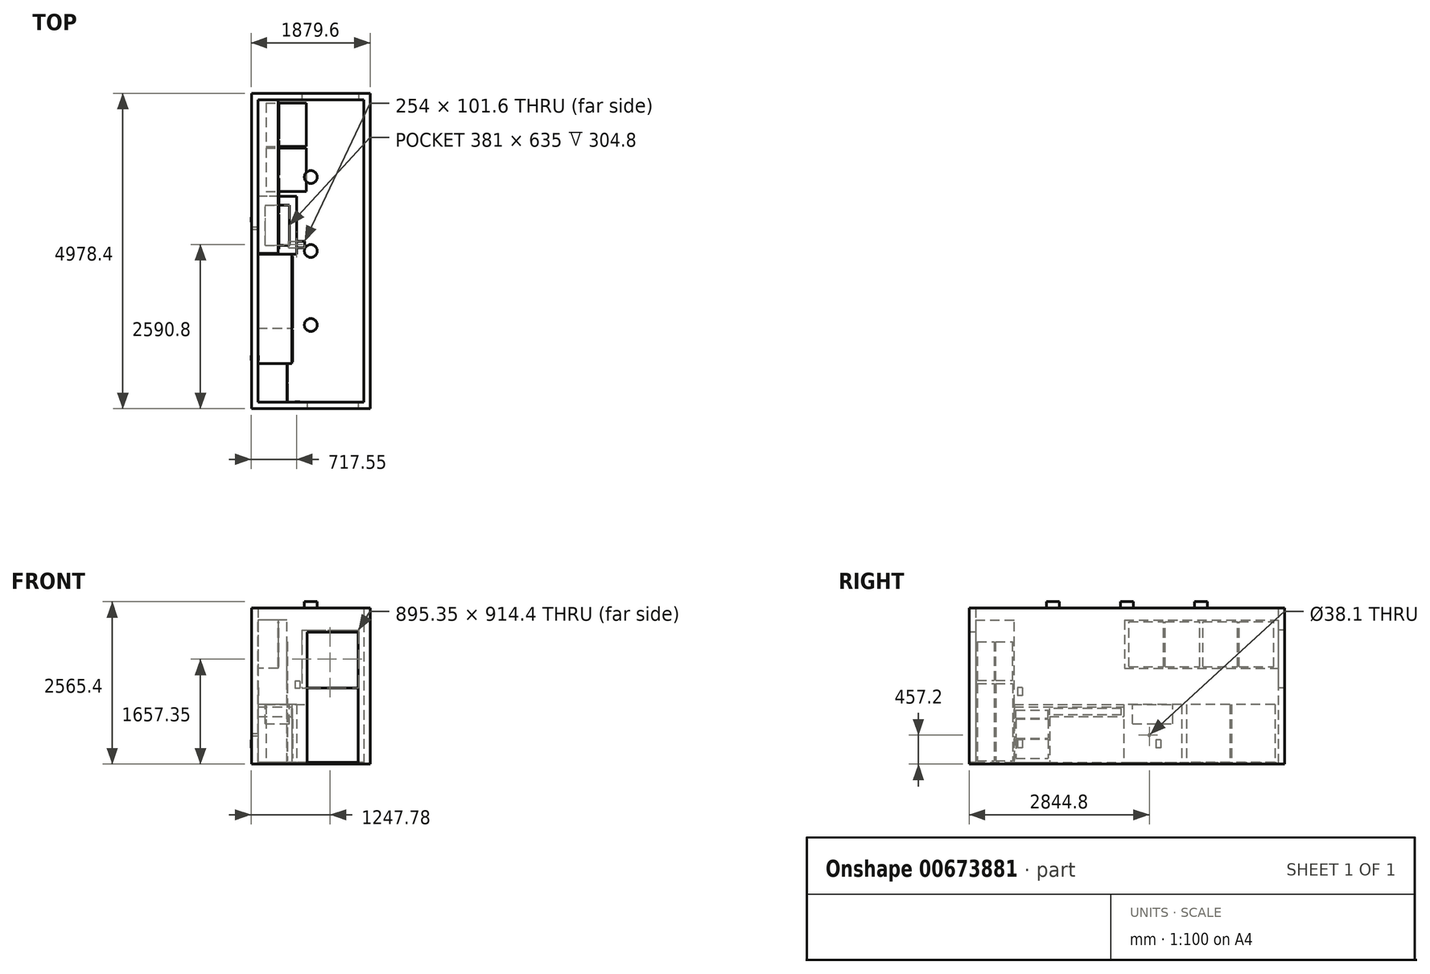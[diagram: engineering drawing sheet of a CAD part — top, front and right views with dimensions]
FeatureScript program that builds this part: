
annotation { "Feature Type Name" : "Feature", "Feature Type Description" : "" }
export const myFeature = defineFeature(function(context is Context, id is Id, definition is map)
    precondition{}
    {
        {
            var Q0;
            Q0=qCreatedBy(makeId("Top.planeOp"),FACE);
            var sketch = newSketch(context, id + "F0", { "sketchPlane" : qUnion([Q0])});
            skLineSegment(sketch, "E0.bottom", {"start": v(0, 0) * mm, "end": v(-1670.05, 0) * mm});
            skLineSegment(sketch, "E0.top", {"start": v(0, 4775.2) * mm, "end": v(-1670.05, 4775.2) * mm});
            skLineSegment(sketch, "E0.left", {"start": v(0, 0) * mm, "end": v(0, 4775.2) * mm});
            skLineSegment(sketch, "E0.right", {"start": v(-1670.05, 0) * mm, "end": v(-1670.05, 4775.2) * mm});
            skLineSegment(sketch, "E1.0", {"start": v(-1771.65, -101.6) * mm, "end": v(-1771.65, 4876.8) * mm});
            skLineSegment(sketch, "E1.1", {"start": v(101.6, -101.6) * mm, "end": v(-1771.65, -101.6) * mm});
            skLineSegment(sketch, "E1.2", {"start": v(101.6, -101.6) * mm, "end": v(101.6, 4876.8) * mm});
            skLineSegment(sketch, "E1.3", {"start": v(101.6, 4876.8) * mm, "end": v(-1771.65, 4876.8) * mm});
            skSolve(sketch);
        }
        {
            var Q0;
            Q0=qSketchRegion(id+"F0",true);
            extrude(context, id + "F1", {"entities" : qUnion([Q0]), "depth" : 2438.4 * mm, "offsetDistance" : 25.4 * mm});
        }
        {
            var Q0;
            Q0=makeQuery(id+"F1.opExtrude","SWEPT_FACE",FACE,{"disambiguationData":[OSD([sQuery(id+"F0.wireOp",EDGE,"E1.1")])]});
            var sketch = newSketch(context, id + "F2", { "sketchPlane" : qUnion([Q0])});
            skLineSegment(sketch, "E2.bottom", {"start": v(-88.9, 0) * mm, "end": v(-895.35, 0) * mm});
            skLineSegment(sketch, "E2.top", {"start": v(-88.9, 2057.4) * mm, "end": v(-895.35, 2057.4) * mm});
            skLineSegment(sketch, "E2.left", {"start": v(-88.9, 0) * mm, "end": v(-88.9, 2057.4) * mm});
            skLineSegment(sketch, "E2.right", {"start": v(-895.35, 0) * mm, "end": v(-895.35, 2057.4) * mm});
            skSolve(sketch);
        }
        {
            var Q0;
            Q0=qSketchRegion(id+"F2",true);
            extrude(context, id + "F3", {"entities" : qUnion([Q0]), "operationType" : NewBodyOperationType.REMOVE, "endBound" : BoundingType.UP_TO_NEXT, "oppositeDirection" : true, "depth" : 25.4 * mm, "offsetDistance" : 25.4 * mm});
        }
        {
            var Q0;
            Q0=makeQuery(id+"F1.opExtrude","SWEPT_FACE",FACE,{"disambiguationData":[OSD([sQuery(id+"F0.wireOp",EDGE,"E0.top")])]});
            var sketch = newSketch(context, id + "F4", { "sketchPlane" : qUnion([Q0])});
            skLineSegment(sketch, "E3.bottom", {"start": v(-977.9, 2089.15) * mm, "end": v(-82.55, 2089.15) * mm});
            skLineSegment(sketch, "E3.top", {"start": v(-977.9, 1174.75) * mm, "end": v(-82.55, 1174.75) * mm});
            skLineSegment(sketch, "E3.left", {"start": v(-977.9, 2089.15) * mm, "end": v(-977.9, 1174.75) * mm});
            skLineSegment(sketch, "E3.right", {"start": v(-82.55, 2089.15) * mm, "end": v(-82.55, 1174.75) * mm});
            skSolve(sketch);
        }
        {
            var Q0;
            Q0=qSketchRegion(id+"F4",true);
            extrude(context, id + "F5", {"entities" : qUnion([Q0]), "operationType" : NewBodyOperationType.REMOVE, "endBound" : BoundingType.UP_TO_NEXT, "oppositeDirection" : true, "depth" : 25.4 * mm, "offsetDistance" : 25.4 * mm});
        }
        {
            var Q0;
            Q0=makeQuery(id+"F1.opExtrude","CAP_FACE",FACE,{"disambiguationData":[OSD([sQuery(id+"F0.wireOp",EDGE,"E0.bottom"),sQuery(id+"F0.wireOp",EDGE,"E0.top"),sQuery(id+"F0.wireOp",EDGE,"E0.left"),sQuery(id+"F0.wireOp",EDGE,"E0.right"),sQuery(id+"F0.wireOp",EDGE,"E1.0"),sQuery(id+"F0.wireOp",EDGE,"E1.1"),sQuery(id+"F0.wireOp",EDGE,"E1.2"),sQuery(id+"F0.wireOp",EDGE,"E1.3")])],"isStart":true});
            var sketch = newSketch(context, id + "F6", { "sketchPlane" : qUnion([Q0])});
            skLineSegment(sketch, "E4.bottom", {"start": v(101.6, 101.6) * mm, "end": v(-1771.65, 101.6) * mm});
            skLineSegment(sketch, "E4.top", {"start": v(101.6, -4876.8) * mm, "end": v(-1771.65, -4876.8) * mm});
            skLineSegment(sketch, "E4.left", {"start": v(101.6, 101.6) * mm, "end": v(101.6, -4876.8) * mm});
            skLineSegment(sketch, "E4.right", {"start": v(-1771.65, 101.6) * mm, "end": v(-1771.65, -4876.8) * mm});
            skLineSegment(sketch, "E5.bottom", {"start": v(-1187.45, -2438.4) * mm, "end": v(-933.45, -2438.4) * mm});
            skLineSegment(sketch, "E5.top", {"start": v(-1187.45, -2540) * mm, "end": v(-933.45, -2540) * mm});
            skLineSegment(sketch, "E5.left", {"start": v(-1187.45, -2438.4) * mm, "end": v(-1187.45, -2540) * mm});
            skLineSegment(sketch, "E5.right", {"start": v(-933.45, -2438.4) * mm, "end": v(-933.45, -2540) * mm});
            skSolve(sketch);
        }
        {
            var Q0;
            Q0=qSketchRegion(id+"F6",true);
            extrude(context, id + "F7", {"entities" : qUnion([Q0]), "operationType" : NewBodyOperationType.ADD, "depth" : 25.4 * mm, "offsetDistance" : 25.4 * mm});
        }
        {
            var Q0;
            Q0=makeQuery(id+"F7.opExtrude","CAP_FACE",FACE,{"disambiguationData":[OSD([sQuery(id+"F6.wireOp",EDGE,"E4.bottom"),sQuery(id+"F6.wireOp",EDGE,"E4.top"),sQuery(id+"F6.wireOp",EDGE,"E4.left"),sQuery(id+"F6.wireOp",EDGE,"E4.right")])],"isStart":true});
            var sketch = newSketch(context, id + "F8", { "sketchPlane" : qUnion([Q0])});
            skLineSegment(sketch, "E6.bottom", {"start": v(-1543.05, 4724.4) * mm, "end": v(-908.05, 4724.4) * mm});
            skLineSegment(sketch, "E6.top", {"start": v(-1543.05, 4038.6) * mm, "end": v(-908.05, 4038.6) * mm});
            skLineSegment(sketch, "E6.left", {"start": v(-1543.05, 4724.4) * mm, "end": v(-1543.05, 4038.6) * mm});
            skLineSegment(sketch, "E6.right", {"start": v(-908.05, 4724.4) * mm, "end": v(-908.05, 4038.6) * mm});
            skLineSegment(sketch, "E7.bottom", {"start": v(-1543.05, 4013.2) * mm, "end": v(-908.05, 4013.2) * mm});
            skLineSegment(sketch, "E7.top", {"start": v(-1543.05, 3327.4) * mm, "end": v(-908.05, 3327.4) * mm});
            skLineSegment(sketch, "E7.left", {"start": v(-1543.05, 4013.2) * mm, "end": v(-1543.05, 3327.4) * mm});
            skLineSegment(sketch, "E7.right", {"start": v(-908.05, 4013.2) * mm, "end": v(-908.05, 3327.4) * mm});
            skSolve(sketch);
        }
        {
            var Q0;
            Q0=qSketchRegion(id+"F8",true);
            extrude(context, id + "F9", {"entities" : qUnion([Q0]), "depth" : 914.4 * mm, "offsetDistance" : 25.4 * mm});
        }
        {
            var Q0;
            {var subQ0=sQuery(id+"F0.wireOp",EDGE,"E0.top");var subQ5=sQuery(id+"F0.wireOp",EDGE,"E0.right");Q0=makeQuery(id+"FF5OUzfLRYdxron_1.boolean.opBoolean","SPLIT",FACE,{"disambiguationData":[TD([makeQuery(id+"F1.opExtrude","SWEPT_FACE",FACE,{"disambiguationData":[OSD([subQ0])]})])],"derivedFrom":makeQuery(id+"F1.opExtrude","SWEPT_FACE",FACE,{"disambiguationData":[OSD([subQ5])]})});}
            var sketch = newSketch(context, id + "F10", { "sketchPlane" : qUnion([Q0])});
            skLineSegment(sketch, "E8.top", {"start": v(2349.5, 1485.9) * mm, "end": v(4775.2, 1485.9) * mm});
            skLineSegment(sketch, "E8.left", {"start": v(2349.5, 2247.9) * mm, "end": v(2349.5, 1485.9) * mm});
            skLineSegment(sketch, "E8.right", {"start": v(4775.2, 2247.9) * mm, "end": v(4775.2, 1485.9) * mm});
            skLineSegment(sketch, "E9", {"start": v(2349.5, 2247.9) * mm, "end": v(4775.2, 2247.9) * mm});
            skSolve(sketch);
        }
        {
            var Q0;
            Q0=qSketchRegion(id+"F10",true);
            extrude(context, id + "F11", {"entities" : qUnion([Q0]), "depth" : 317.5 * mm, "offsetDistance" : 25.4 * mm});
        }
        {
            var Q0;
            Q0=makeQuery(id+"F7.boolean.opBoolean","MERGE",FACE,{"derivedFrom":[makeQuery(id+"F1.opExtrude","SWEPT_FACE",FACE,{"disambiguationData":[OSD([sQuery(id+"F0.wireOp",EDGE,"E1.0")])]}),makeQuery(id+"F7.opExtrude","SWEPT_FACE",FACE,{"disambiguationData":[OSD([sQuery(id+"F6.wireOp",EDGE,"E4.right")])]})]});
            var sketch = newSketch(context, id + "F12", { "sketchPlane" : qUnion([Q0])});
            skCircle(sketch, "E10", {"center": v(-2743.2, 431.8) * mm, "radius": 19.05 * mm});
            skSolve(sketch);
        }
        {
            var Q0;
            Q0=makeQuery(id+"F1.opExtrude","SWEPT_FACE",FACE,{"disambiguationData":[OSD([sQuery(id+"F0.wireOp",EDGE,"E0.bottom")])]});
            var sketch = newSketch(context, id + "F13", { "sketchPlane" : qUnion([Q0])});
            skLineSegment(sketch, "E11.bottom", {"start": v(1009.65, 1282.7) * mm, "end": v(1085.85, 1282.7) * mm});
            skLineSegment(sketch, "E11.top", {"start": v(1009.65, 1168.4) * mm, "end": v(1085.85, 1168.4) * mm});
            skLineSegment(sketch, "E11.left", {"start": v(1009.65, 1282.7) * mm, "end": v(1009.65, 1168.4) * mm});
            skLineSegment(sketch, "E11.right", {"start": v(1085.85, 1282.7) * mm, "end": v(1085.85, 1168.4) * mm});
            skSolve(sketch);
        }
        {
            var Q0;
            Q0=qSketchRegion(id+"F13",true);
            extrude(context, id + "F14", {"entities" : qUnion([Q0]), "depth" : 6.35 * mm, "offsetDistance" : 25.4 * mm});
        }
        {
            var Q0;
            {var subQ0=sQuery(id+"F0.wireOp",EDGE,"E1.3");var subQ1=sQuery(id+"F0.wireOp",EDGE,"E1.2");var subQ2=sQuery(id+"F0.wireOp",EDGE,"E1.1");var subQ3=sQuery(id+"F0.wireOp",EDGE,"E1.0");var subQ4=sQuery(id+"F0.wireOp",EDGE,"E0.right");var subQ5=sQuery(id+"F0.wireOp",EDGE,"E0.left");var subQ6=sQuery(id+"F0.wireOp",EDGE,"E0.top");var subQ7=sQuery(id+"F0.wireOp",EDGE,"E0.bottom");Q0=makeQuery(id+"F6lEAw4BziHLS6e_1.boolean.opBoolean","MERGE",FACE,{"derivedFrom":[makeQuery(id+"FF5OUzfLRYdxron_1.boolean.opBoolean","MERGE",FACE,{"derivedFrom":[makeQuery(id+"F1.opExtrude","CAP_FACE",FACE,{"disambiguationData":[OSD([subQ7,subQ6,subQ5,subQ4,subQ3,subQ2,subQ1,subQ0])],"isStart":false}),makeQuery(id+"FF5OUzfLRYdxron_1.opExtrude","CAP_FACE",FACE,{"disambiguationData":[OSD([subQ7,subQ6,subQ5,subQ4,subQ3,subQ2,subQ1,subQ0]),OD(0.0)],"isStart":false}),makeQuery(id+"FF5OUzfLRYdxron_1.opExtrude","CAP_FACE",FACE,{"disambiguationData":[OSD([subQ7,subQ6,subQ5,subQ4,subQ3,subQ2,subQ1,subQ0]),OD(1.0)],"isStart":false})]}),makeQuery(id+"F6lEAw4BziHLS6e_1.opExtrude","SWEPT_FACE",FACE,{"disambiguationData":[OSD([sQuery(id+"FKdh9NI14bl7I8A_1.wireOp",EDGE,"L0rorLmK-Bkry-kT8l-oB2h-IIx823DkUJX5.bottom")])]})]});}
            var sketch = newSketch(context, id + "F15", { "sketchPlane" : qUnion([Q0])});
            skCircle(sketch, "E12", {"center": v(-835.03, 3556) * mm, "radius": 101.6 * mm});
            skCircle(sketch, "E13", {"center": v(-835.03, 1219.2) * mm, "radius": 101.6 * mm});
            skLineSegment(sketch, "E14", {"start": v(-1670.05, 3556) * mm, "end": v(-835.03, 3556) * mm, "construction": true});
            skLineSegment(sketch, "E15", {"start": v(0, 3556) * mm, "end": v(-835.03, 3556) * mm, "construction": true});
            skLineSegment(sketch, "E16", {"start": v(0, 1219.2) * mm, "end": v(-1670.05, 1219.2) * mm, "construction": true});
            skLineSegment(sketch, "E17", {"start": v(-835.03, 1219.2) * mm, "end": v(-835.03, 0) * mm, "construction": true});
            skCircle(sketch, "E18", {"center": v(-835.03, 2387.6) * mm, "radius": 101.6 * mm});
            skLineSegment(sketch, "E19", {"start": v(-835.03, 1219.2) * mm, "end": v(-835.03, 3556) * mm, "construction": true});
            skSolve(sketch);
        }
        {
            var Q0;
            Q0=qSketchRegion(id+"F15",true);
            extrude(context, id + "F16", {"entities" : qUnion([Q0]), "depth" : 101.6 * mm, "offsetDistance" : 25.4 * mm});
        }
        {
            var Q0;
            Q0=makeQuery(id+"F1.opExtrude","SWEPT_FACE",FACE,{"disambiguationData":[OSD([sQuery(id+"F0.wireOp",EDGE,"E0.right")])]});
            var sketch = newSketch(context, id + "F17", { "sketchPlane" : qUnion([Q0])});
            skLineSegment(sketch, "E20.bottom", {"start": v(0, 0) * mm, "end": v(609.6, 0) * mm});
            skLineSegment(sketch, "E20.top", {"start": v(0, 2438.4) * mm, "end": v(0, 2438.4) * mm});
            skLineSegment(sketch, "E20.left", {"start": v(0, 0) * mm, "end": v(0, 2438.4) * mm});
            skLineSegment(sketch, "E20.right", {"start": v(609.6, 0) * mm, "end": v(609.6, 2247.9) * mm});
            skLineSegment(sketch, "E21", {"start": v(0, 2247.9) * mm, "end": v(0, 0) * mm});
            skLineSegment(sketch, "E22", {"start": v(0, 2247.9) * mm, "end": v(609.6, 2247.9) * mm});
            skSolve(sketch);
        }
        {
            var Q0;
            {var subQ0=sQuery(id+"F17.wireOp",EDGE,"E20.right");Q0=makeQuery(id+"F17.imprint","IMPRINT",FACE,{"disambiguationData":[TD([[makeQuery(id+"F17.imprint","IMPRINT",EDGE,{"derivedFrom":subQ0}),1.0]])]});}
            extrude(context, id + "F18", {"entities" : qUnion([Q0]), "depth" : 457.2 * mm, "offsetDistance" : 25.4 * mm});
        }
        {
            var Q0;
            Q0=makeQuery(id+"F1.opExtrude","SWEPT_FACE",FACE,{"disambiguationData":[OSD([sQuery(id+"F0.wireOp",EDGE,"E0.right")])]});
            var sketch = newSketch(context, id + "F19", { "sketchPlane" : qUnion([Q0])});
            skLineSegment(sketch, "E23.bottom", {"start": v(3251.2, 914.4) * mm, "end": v(2336.8, 914.4) * mm});
            skLineSegment(sketch, "E23.top", {"start": v(3251.2, 0) * mm, "end": v(2336.8, 0) * mm});
            skLineSegment(sketch, "E23.left", {"start": v(3251.2, 914.4) * mm, "end": v(3251.2, 0) * mm});
            skLineSegment(sketch, "E23.right", {"start": v(2336.8, 914.4) * mm, "end": v(2336.8, 0) * mm});
            skSolve(sketch);
        }
        {
            var Q0;
            Q0 = qSketchRegion(id + "F19", true);
            extrude(context, id + "F20", {"entities" : qUnion([Q0]), "depth" : 609.6 * mm, "offsetDistance" : 25.4 * mm});
        }
        {
            var Q0;
            Q0=makeQuery(id+"F1.opExtrude","SWEPT_FACE",FACE,{"disambiguationData":[OSD([sQuery(id+"F0.wireOp",EDGE,"E0.right")])]});
            var sketch = newSketch(context, id + "F21", { "sketchPlane" : qUnion([Q0])});
            skLineSegment(sketch, "E24.0.0", {"start": v(609.6, 0) * mm, "end": v(609.6, 0) * mm});
            skLineSegment(sketch, "E24.0.2", {"start": v(609.6, 0) * mm, "end": v(609.6, 0) * mm});
            skLineSegment(sketch, "E25.bottom", {"start": v(609.6, 914.4) * mm, "end": v(2336.8, 914.4) * mm});
            skLineSegment(sketch, "E25.top", {"start": v(609.6, 876.3) * mm, "end": v(2336.8, 876.3) * mm});
            skLineSegment(sketch, "E25.left", {"start": v(609.6, 914.4) * mm, "end": v(609.6, 876.3) * mm});
            skLineSegment(sketch, "E25.right", {"start": v(2336.8, 914.4) * mm, "end": v(2336.8, 876.3) * mm});
            skSolve(sketch);
        }
        {
            var Q0;
            Q0 = qSketchRegion(id + "F21", true);
            extrude(context, id + "F22", {"entities" : qUnion([Q0]), "depth" : 533.4 * mm, "offsetDistance" : 25.4 * mm});
        }
        {
            var Q0;
            Q0=makeQuery(id+"FyeGjvqHZ8qtpXd_9.boolean.opBoolean","MERGE",FACE,{"derivedFrom":[makeQuery(id+"F22.opExtrude","CAP_FACE",FACE,{"disambiguationData":[OSD([sQuery(id+"F21.wireOp",EDGE,"E25.bottom"),sQuery(id+"F21.wireOp",EDGE,"E25.top"),sQuery(id+"F21.wireOp",EDGE,"E25.left"),sQuery(id+"F21.wireOp",EDGE,"E25.right")])],"isStart":false}),makeQuery(id+"FyeGjvqHZ8qtpXd_9.opExtrude","SWEPT_FACE",FACE,{"disambiguationData":[OSD([sQuery(id+"F46rnMOmZh9QJuk_9.wireOp",EDGE,"LmVa3B9K-5IW6-0650-ylxf-dCjXZTulEtGs.left")])]})]});
            var sketch = newSketch(context, id + "F23", { "sketchPlane" : qUnion([Q0])});
            skLineSegment(sketch, "E26.bottom", {"start": v(609.6, 876.3) * mm, "end": v(1168.4, 876.3) * mm});
            skLineSegment(sketch, "E26.top", {"start": v(609.6, 0) * mm, "end": v(1168.4, 0) * mm});
            skLineSegment(sketch, "E26.left", {"start": v(609.6, 876.3) * mm, "end": v(609.6, 0) * mm});
            skLineSegment(sketch, "E26.right", {"start": v(1168.4, 876.3) * mm, "end": v(1168.4, 0) * mm});
            skLineSegment(sketch, "E27.0", {"start": v(2336.8, 914.4) * mm, "end": v(2336.8, 0) * mm});
            skLineSegment(sketch, "E28.bottom", {"start": v(1168.4, 876.3) * mm, "end": v(2336.8, 876.3) * mm});
            skLineSegment(sketch, "E28.top", {"start": v(1168.4, 723.9) * mm, "end": v(2336.8, 723.9) * mm});
            skLineSegment(sketch, "E28.left", {"start": v(1168.4, 876.3) * mm, "end": v(1168.4, 723.9) * mm});
            skLineSegment(sketch, "E28.right", {"start": v(2336.8, 876.3) * mm, "end": v(2336.8, 723.9) * mm});
            skSolve(sketch);
        }
        {
            var Q0;
            Q0 = qSketchRegion(id + "F23", true);
            extrude(context, id + "F24", {"entities" : qUnion([Q0]), "endBound" : BoundingType.UP_TO_NEXT, "oppositeDirection" : true, "depth" : 25.4 * mm, "offsetDistance" : 25.4 * mm});
        }
        {
            var Q0;
            Q0=makeQuery(id+"F24.opExtrude","CAP_FACE",FACE,{"disambiguationData":[OSD([sQuery(id+"F23.wireOp",EDGE,"E26.bottom"),sQuery(id+"F23.wireOp",EDGE,"E26.top"),sQuery(id+"F23.wireOp",EDGE,"E26.left"),sQuery(id+"F23.wireOp",EDGE,"E26.right")])],"isStart":true});
            var sketch = newSketch(context, id + "F25", { "sketchPlane" : qUnion([Q0])});
            skLineSegment(sketch, "E29.bottom", {"start": v(635, 368.3) * mm, "end": v(1143, 368.3) * mm});
            skLineSegment(sketch, "E29.top", {"start": v(635, 63.5) * mm, "end": v(1143, 63.5) * mm});
            skLineSegment(sketch, "E29.left", {"start": v(635, 368.3) * mm, "end": v(635, 63.5) * mm});
            skLineSegment(sketch, "E29.right", {"start": v(1143, 368.3) * mm, "end": v(1143, 63.5) * mm});
            skLineSegment(sketch, "E30.bottom", {"start": v(635, 685.8) * mm, "end": v(1143, 685.8) * mm});
            skLineSegment(sketch, "E30.top", {"start": v(635, 381) * mm, "end": v(1143, 381) * mm});
            skLineSegment(sketch, "E30.left", {"start": v(635, 685.8) * mm, "end": v(635, 381) * mm});
            skLineSegment(sketch, "E30.right", {"start": v(1143, 685.8) * mm, "end": v(1143, 381) * mm});
            skLineSegment(sketch, "E31.bottom", {"start": v(635, 698.5) * mm, "end": v(1143, 698.5) * mm});
            skLineSegment(sketch, "E31.top", {"start": v(635, 825.5) * mm, "end": v(1143, 825.5) * mm});
            skLineSegment(sketch, "E31.left", {"start": v(635, 698.5) * mm, "end": v(635, 825.5) * mm});
            skLineSegment(sketch, "E31.right", {"start": v(1143, 698.5) * mm, "end": v(1143, 825.5) * mm});
            skLineSegment(sketch, "E32", {"start": v(1143, 698.5) * mm, "end": v(1143, 685.8) * mm, "construction": true});
            skLineSegment(sketch, "E33", {"start": v(1143, 381) * mm, "end": v(1143, 368.3) * mm, "construction": true});
            skLineSegment(sketch, "E34", {"start": v(609.6, 825.5) * mm, "end": v(635, 825.5) * mm, "construction": true});
            skLineSegment(sketch, "E35", {"start": v(1143, 825.5) * mm, "end": v(1168.4, 825.5) * mm, "construction": true});
            skLineSegment(sketch, "E36.left", {"start": v(1168.4, 0) * mm, "end": v(1168.4, -177.8) * mm});
            skLineSegment(sketch, "E37.bottom", {"start": v(2302.58, 750.93) * mm, "end": v(1168.4, 750.93) * mm});
            skLineSegment(sketch, "E37.top", {"start": v(2302.58, 855.12) * mm, "end": v(1168.4, 855.12) * mm});
            skLineSegment(sketch, "E37.left", {"start": v(2302.58, 750.93) * mm, "end": v(2302.58, 855.12) * mm});
            skLineSegment(sketch, "E37.right", {"start": v(1168.4, 750.93) * mm, "end": v(1168.4, 855.12) * mm});
            skSolve(sketch);
        }
        {
            var Q0;
            Q0 = qSketchRegion(id + "F25", true);
            extrude(context, id + "F26", {"entities" : qUnion([Q0]), "operationType" : NewBodyOperationType.ADD, "depth" : 12.7 * mm, "offsetDistance" : 25.4 * mm});
        }
        {
            var Q0;
            Q0 = qSketchRegion(id + "F12", true);
            var Q1;
            Q1=makeQuery(id+"F1.opExtrude","SWEPT_FACE",FACE,{"disambiguationData":[OSD([sQuery(id+"F0.wireOp",EDGE,"E0.right")])]});
            extrude(context, id + "F27", {"entities" : qUnion([Q0]), "operationType" : NewBodyOperationType.REMOVE, "endBound" : BoundingType.UP_TO_SURFACE, "oppositeDirection" : true, "depth" : 25.4 * mm, "endBoundEntityFace" : qUnion([Q1]), "offsetDistance" : 25.4 * mm});
        }
        {
            var Q0;
            Q0=makeQuery(id+"F18.opExtrude","CAP_FACE",FACE,{"disambiguationData":[OSD([sQuery(id+"F17.wireOp",EDGE,"E20.bottom"),sQuery(id+"F17.wireOp",EDGE,"E20.top"),sQuery(id+"F17.wireOp",EDGE,"E20.right"),sQuery(id+"F17.wireOp",EDGE,"E21")])],"isStart":false});
            var sketch = newSketch(context, id + "F28", { "sketchPlane" : qUnion([Q0])});
            skLineSegment(sketch, "E38.bottom", {"start": v(25.4, 1244.6) * mm, "end": v(292.1, 1244.6) * mm});
            skLineSegment(sketch, "E38.top", {"start": v(25.4, 25.4) * mm, "end": v(292.1, 25.4) * mm});
            skLineSegment(sketch, "E38.left", {"start": v(25.4, 1244.6) * mm, "end": v(25.4, 25.4) * mm});
            skLineSegment(sketch, "E38.right", {"start": v(292.1, 1244.6) * mm, "end": v(292.1, 25.4) * mm});
            skLineSegment(sketch, "E39.bottom", {"start": v(317.5, 1244.6) * mm, "end": v(584.2, 1244.6) * mm});
            skLineSegment(sketch, "E39.top", {"start": v(317.5, 25.4) * mm, "end": v(584.2, 25.4) * mm});
            skLineSegment(sketch, "E39.left", {"start": v(317.5, 1244.6) * mm, "end": v(317.5, 25.4) * mm});
            skLineSegment(sketch, "E39.right", {"start": v(584.2, 1244.6) * mm, "end": v(584.2, 25.4) * mm});
            skLineSegment(sketch, "E40.bottom", {"start": v(25.4, 1905) * mm, "end": v(292.1, 1905) * mm});
            skLineSegment(sketch, "E40.top", {"start": v(25.4, 1295.4) * mm, "end": v(292.1, 1295.4) * mm});
            skLineSegment(sketch, "E40.left", {"start": v(25.4, 1905) * mm, "end": v(25.4, 1295.4) * mm});
            skLineSegment(sketch, "E40.right", {"start": v(292.1, 1905) * mm, "end": v(292.1, 1295.4) * mm});
            skLineSegment(sketch, "E41.bottom", {"start": v(317.5, 1295.4) * mm, "end": v(584.2, 1295.4) * mm});
            skLineSegment(sketch, "E41.top", {"start": v(317.5, 1905) * mm, "end": v(584.2, 1905) * mm});
            skLineSegment(sketch, "E41.left", {"start": v(317.5, 1295.4) * mm, "end": v(317.5, 1905) * mm});
            skLineSegment(sketch, "E41.right", {"start": v(584.2, 1295.4) * mm, "end": v(584.2, 1905) * mm});
            skSolve(sketch);
        }
        {
            var Q0;
            Q0 = qSketchRegion(id + "F28", true);
            extrude(context, id + "F29", {"entities" : qUnion([Q0]), "operationType" : NewBodyOperationType.ADD, "depth" : 6.35 * mm, "offsetDistance" : 25.4 * mm});
        }
        {
            var Q0;
            Q0=makeQuery(id+"F11.opExtrude","CAP_FACE",FACE,{"disambiguationData":[OSD([sQuery(id+"F10.wireOp",EDGE,"E8.top"),sQuery(id+"F10.wireOp",EDGE,"E8.left"),sQuery(id+"F10.wireOp",EDGE,"E8.right"),sQuery(id+"F10.wireOp",EDGE,"E9")])],"isStart":false});
            var sketch = newSketch(context, id + "F30", { "sketchPlane" : qUnion([Q0])});
            skLineSegment(sketch, "E42.bottom", {"start": v(2419.35, 1511.3) * mm, "end": v(2965.45, 1511.3) * mm});
            skLineSegment(sketch, "E42.top", {"start": v(2419.35, 2222.5) * mm, "end": v(2965.45, 2222.5) * mm});
            skLineSegment(sketch, "E42.left", {"start": v(2419.35, 1511.3) * mm, "end": v(2419.35, 2222.5) * mm});
            skLineSegment(sketch, "E42.right", {"start": v(2965.45, 1511.3) * mm, "end": v(2965.45, 2222.5) * mm});
            skLineSegment(sketch, "E43.bottom", {"start": v(2990.85, 1511.3) * mm, "end": v(3536.95, 1511.3) * mm});
            skLineSegment(sketch, "E43.top", {"start": v(2990.85, 2222.5) * mm, "end": v(3536.95, 2222.5) * mm});
            skLineSegment(sketch, "E43.left", {"start": v(2990.85, 1511.3) * mm, "end": v(2990.85, 2222.5) * mm});
            skLineSegment(sketch, "E43.right", {"start": v(3536.95, 1511.3) * mm, "end": v(3536.95, 2222.5) * mm});
            skLineSegment(sketch, "E44.bottom", {"start": v(3587.75, 1511.3) * mm, "end": v(4133.85, 1511.3) * mm});
            skLineSegment(sketch, "E44.top", {"start": v(3587.75, 2222.5) * mm, "end": v(4133.85, 2222.5) * mm});
            skLineSegment(sketch, "E44.left", {"start": v(3587.75, 1511.3) * mm, "end": v(3587.75, 2222.5) * mm});
            skLineSegment(sketch, "E44.right", {"start": v(4133.85, 1511.3) * mm, "end": v(4133.85, 2222.5) * mm});
            skLineSegment(sketch, "E45.bottom", {"start": v(4159.25, 1511.3) * mm, "end": v(4705.35, 1511.3) * mm});
            skLineSegment(sketch, "E45.top", {"start": v(4159.25, 2222.5) * mm, "end": v(4705.35, 2222.5) * mm});
            skLineSegment(sketch, "E45.left", {"start": v(4159.25, 1511.3) * mm, "end": v(4159.25, 2222.5) * mm});
            skLineSegment(sketch, "E45.right", {"start": v(4705.35, 1511.3) * mm, "end": v(4705.35, 2222.5) * mm});
            skSolve(sketch);
        }
        {
            var Q0;
            Q0 = qSketchRegion(id + "F30", true);
            extrude(context, id + "F31", {"entities" : qUnion([Q0]), "operationType" : NewBodyOperationType.ADD, "depth" : 12.7 * mm, "offsetDistance" : 25.4 * mm});
        }
        {
            var Q0;
            Q0=makeQuery(id+"F7.boolean.opBoolean","MERGE",FACE,{"derivedFrom":[makeQuery(id+"F1.opExtrude","SWEPT_FACE",FACE,{"disambiguationData":[OSD([sQuery(id+"F0.wireOp",EDGE,"E1.0")])]}),makeQuery(id+"F7.opExtrude","SWEPT_FACE",FACE,{"disambiguationData":[OSD([sQuery(id+"F6.wireOp",EDGE,"E4.right")])]})]});
            var sketch = newSketch(context, id + "F32", { "sketchPlane" : qUnion([Q0])});
            skLineSegment(sketch, "E46.bottom", {"start": v(-736.6, 355.6) * mm, "end": v(-660.4, 355.6) * mm});
            skLineSegment(sketch, "E46.top", {"start": v(-736.6, 228.6) * mm, "end": v(-660.4, 228.6) * mm});
            skLineSegment(sketch, "E46.left", {"start": v(-736.6, 355.6) * mm, "end": v(-736.6, 228.6) * mm});
            skLineSegment(sketch, "E46.right", {"start": v(-660.4, 355.6) * mm, "end": v(-660.4, 228.6) * mm});
            skLineSegment(sketch, "E47.bottom", {"start": v(-2921, 355.6) * mm, "end": v(-2844.8, 355.6) * mm});
            skLineSegment(sketch, "E47.top", {"start": v(-2921, 228.6) * mm, "end": v(-2844.8, 228.6) * mm});
            skLineSegment(sketch, "E47.left", {"start": v(-2921, 355.6) * mm, "end": v(-2921, 228.6) * mm});
            skLineSegment(sketch, "E47.right", {"start": v(-2844.8, 355.6) * mm, "end": v(-2844.8, 228.6) * mm});
            skSolve(sketch);
        }
        {
            var Q0;
            Q0 = qSketchRegion(id + "F32", true);
            extrude(context, id + "F33", {"entities" : qUnion([Q0]), "depth" : 6.35 * mm, "offsetDistance" : 25.4 * mm});
        }
        {
            var Q0;
            Q0=makeQuery(id+"F1.opExtrude","SWEPT_FACE",FACE,{"disambiguationData":[OSD([sQuery(id+"F0.wireOp",EDGE,"E0.right")])]});
            var sketch = newSketch(context, id + "F34", { "sketchPlane" : qUnion([Q0])});
            skLineSegment(sketch, "E48.0.0", {"start": v(4876.8, 2438.4) * mm, "end": v(4876.8, -25.4) * mm});
            skLineSegment(sketch, "E48.0.1", {"start": v(4876.8, -25.4) * mm, "end": v(-101.6, -25.4) * mm});
            skLineSegment(sketch, "E48.0.2", {"start": v(-101.6, -25.4) * mm, "end": v(-101.6, 2438.4) * mm});
            skLineSegment(sketch, "E48.0.3", {"start": v(-101.6, 2438.4) * mm, "end": v(4876.8, 2438.4) * mm});
            skLineSegment(sketch, "E49.0.0", {"start": v(736.6, 355.6) * mm, "end": v(736.6, 228.6) * mm});
            skLineSegment(sketch, "E49.0.1", {"start": v(736.6, 228.6) * mm, "end": v(660.4, 228.6) * mm});
            skLineSegment(sketch, "E49.0.2", {"start": v(660.4, 228.6) * mm, "end": v(660.4, 355.6) * mm});
            skLineSegment(sketch, "E49.0.3", {"start": v(660.4, 355.6) * mm, "end": v(736.6, 355.6) * mm});
            skLineSegment(sketch, "E49.1.0", {"start": v(2921, 355.6) * mm, "end": v(2921, 228.6) * mm});
            skLineSegment(sketch, "E49.1.1", {"start": v(2921, 228.6) * mm, "end": v(2844.8, 228.6) * mm});
            skLineSegment(sketch, "E49.1.2", {"start": v(2844.8, 228.6) * mm, "end": v(2844.8, 355.6) * mm});
            skLineSegment(sketch, "E49.1.3", {"start": v(2844.8, 355.6) * mm, "end": v(2921, 355.6) * mm});
            skLineSegment(sketch, "E50.bottom", {"start": v(736.6, 1181.1) * mm, "end": v(660.4, 1181.1) * mm});
            skLineSegment(sketch, "E50.top", {"start": v(736.6, 1054.1) * mm, "end": v(660.4, 1054.1) * mm});
            skLineSegment(sketch, "E50.left", {"start": v(736.6, 1181.1) * mm, "end": v(736.6, 1054.1) * mm});
            skLineSegment(sketch, "E50.right", {"start": v(660.4, 1181.1) * mm, "end": v(660.4, 1054.1) * mm});
            skSolve(sketch);
        }
        {
            var Q0;
            Q0=makeQuery(id+"F34.imprint","IMPRINT",FACE,{"disambiguationData":[TD([[makeQuery(id+"F34.imprint","IMPRINT",EDGE,{"derivedFrom":sQuery(id+"F34.wireOp",EDGE,"E50.bottom")}),1.0]])]});
            var Q1;
            Q1=makeQuery(id+"F34.imprint","IMPRINT",FACE,{"disambiguationData":[TD([[makeQuery(id+"F34.imprint","IMPRINT",EDGE,{"derivedFrom":sQuery(id+"F34.wireOp",EDGE,"dTHng7YZ-kgVO-5EVL-SGPU-sYMJY3GJTkV8.bottom")}),-1.0]])]});
            extrude(context, id + "F35", {"entities" : qUnion([Q0, Q1]), "depth" : 6.35 * mm, "offsetDistance" : 25.4 * mm});
        }
        {
            var Q0;
            Q0=makeQuery(id+"F20.opExtrude","SWEPT_FACE",FACE,{"disambiguationData":[OSD([sQuery(id+"F19.wireOp",EDGE,"E23.bottom")])]});
            var sketch = newSketch(context, id + "F36", { "sketchPlane" : qUnion([Q0])});
            skLineSegment(sketch, "E51.bottom", {"start": v(-1555.75, 2476.5) * mm, "end": v(-1174.75, 2476.5) * mm});
            skLineSegment(sketch, "E51.top", {"start": v(-1555.75, 3111.5) * mm, "end": v(-1174.75, 3111.5) * mm});
            skLineSegment(sketch, "E51.left", {"start": v(-1555.75, 2476.5) * mm, "end": v(-1555.75, 3111.5) * mm});
            skLineSegment(sketch, "E51.right", {"start": v(-1174.75, 2476.5) * mm, "end": v(-1174.75, 3111.5) * mm});
            skLineSegment(sketch, "E52", {"start": v(-1365.25, 2336.8) * mm, "end": v(-1365.25, 2476.5) * mm, "construction": true});
            skLineSegment(sketch, "E53", {"start": v(-1060.45, 2794) * mm, "end": v(-1174.75, 2794) * mm, "construction": true});
            skSolve(sketch);
        }
        {
            var Q0;
            Q0 = qSketchRegion(id + "F36", true);
            extrude(context, id + "F37", {"entities" : qUnion([Q0]), "operationType" : NewBodyOperationType.REMOVE, "oppositeDirection" : true, "depth" : 304.8 * mm, "offsetDistance" : 25.4 * mm});
        }
    });
